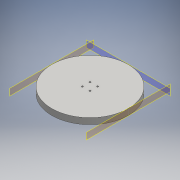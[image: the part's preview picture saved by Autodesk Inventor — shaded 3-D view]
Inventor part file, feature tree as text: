
AUTODESK INVENTOR PART (.ipt)
format: ipt  version: 2016 (Build 200138000, 138)  size: 107,520 bytes
history: native  units: mm
features: other x4, extrude x2, sketch x2
ambient origin geometry x8: Origin, YZ Plane, XZ Plane, XY Plane, X Axis, Y Axis, Z Axis, Center Point
bodies: Body1 (feature_tree)
feature tree (8):
  other  "ソリッド1"
  extrude  "押し出し1"  Depth=101.0mm
  extrude  "押し出し2"  Depth=8.0mm TaperAngle=0.0deg
  other  "作業平面1"
  other  "作業平面2"
  other  "作業平面3"
  sketch  "スケッチ1"
  sketch  "スケッチ2"
